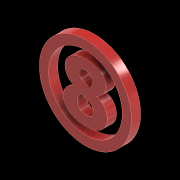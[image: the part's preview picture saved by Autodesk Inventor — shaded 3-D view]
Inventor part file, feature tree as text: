
AUTODESK INVENTOR PART (.ipt)
format: ipt  version: 2020 (Build 240168000, 168)  size: 188,928 bytes
history: native  units: mm
features: other x5, extrude x2, sketch x2
ambient origin geometry x8: Origin, YZ Plane, XZ Plane, XY Plane, X Axis, Y Axis, Z Axis, Center Point
bodies: Body1 (feature_tree)
feature tree (9):
  other  "自動販賣機.ipt"
  extrude  "擠出1"  Depth=10.0mm
  extrude  "擠出2"  Depth=10.0mm TaperAngle=0.0deg
  other  "實體49::自動販賣機.ipt"
  other  "標籤特徵1"
  sketch  "草圖1"
  sketch  "草圖2"
  other  "實體1"
  other  "投影切割邊1"
